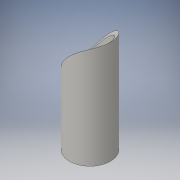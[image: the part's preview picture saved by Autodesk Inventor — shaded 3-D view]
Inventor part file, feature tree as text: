
AUTODESK INVENTOR PART (.ipt)
format: ipt  version: 2016 (Build 200138000, 138)  size: 117,760 bytes
history: native  units: in
note: dims shown in document units (in); Inventor stores cm internally (conversion verified against a paired STEP export)
features: plane x4, extrude x2, sketch x2
ambient origin geometry x8: Origin, YZ Plane, XZ Plane, XY Plane, X Axis, Y Axis, Z Axis, Center Point
bodies: Solid1 (feature_tree)
feature tree (8):
  extrude  "Extrusion1"  Depth=2.376in
  plane  "Work Plane4"
  extrude  "Extrusion2"  Depth=6.0in
  sketch  "Sketch1"  dims[d0=2.0395in d1=2.376in]
  plane  "Work Plane1"
  plane  "Work Plane2"
  plane  "Work Plane3"
  sketch  "Sketch2"  dims[d2=6.0in d3=0.0in d4=3.0in d5=0.84in d6=2.248in d7=2.248in d8=4.496in d9=6.0in d10=0.0in]
